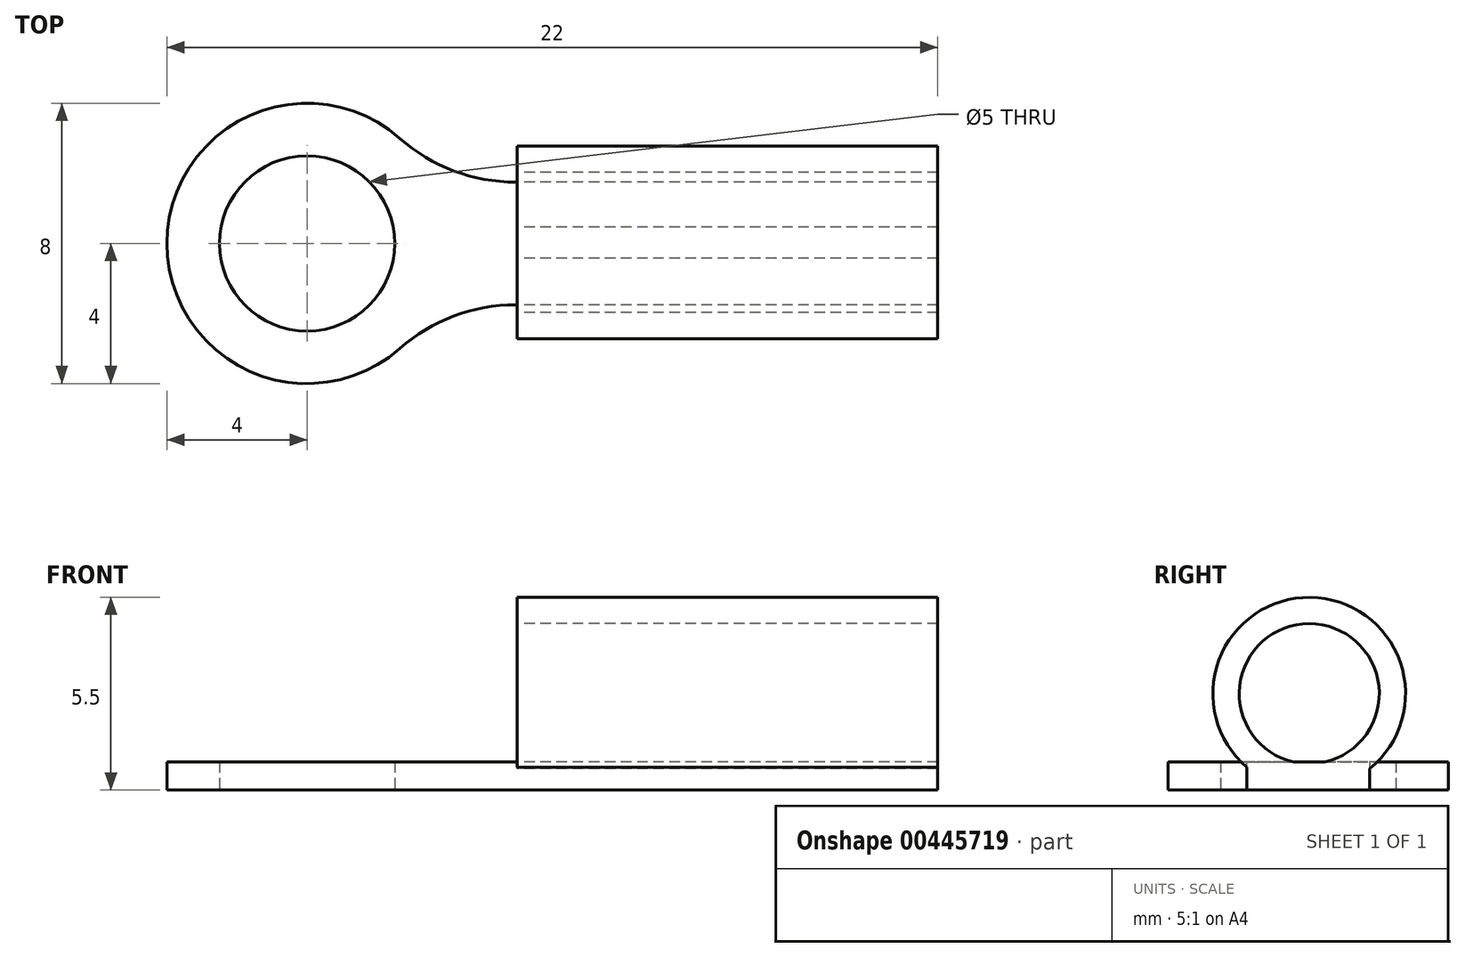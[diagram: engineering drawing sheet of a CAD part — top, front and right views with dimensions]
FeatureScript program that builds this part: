
annotation { "Feature Type Name" : "Feature", "Feature Type Description" : "" }
export const myFeature = defineFeature(function(context is Context, id is Id, definition is map)
    precondition{}
    {
        {
            var Q0;
            Q0=qCreatedBy(makeId("Top.planeOp"),FACE);
            var sketch = newSketch(context, id + "F0", { "sketchPlane" : qUnion([Q0])});
            skCircle(sketch, "E0", {"center": v(0, 0) * mm, "radius": 2.5 * mm});
            skArc(sketch, "E1", {"start": v(2.65, 3) * mm, "mid": v(-4, 0) * mm, "end": v(2.65, -3) * mm});
            skLineSegment(sketch, "E2.bottom", {"start": v(18, 1.75) * mm, "end": v(5.95, 1.75) * mm});
            skLineSegment(sketch, "E2.top", {"start": v(18, -1.75) * mm, "end": v(5.95, -1.75) * mm});
            skLineSegment(sketch, "E2.left", {"start": v(18, 1.75) * mm, "end": v(18, -1.75) * mm});
            skPoint(sketch, "E2.right.end.orphan", {"position": v(-18, -1.75) * mm});
            skPoint(sketch, "E2.right.start.orphan", {"position": v(-18, 1.75) * mm});
            skPoint(sketch, "E3.visualSharp", {"position": v(3.6, 1.75) * mm});
            skArc(sketch, "E3.filletArc", {"start": v(2.65, 3) * mm, "mid": v(4.19, 2.07) * mm, "end": v(5.95, 1.75) * mm});
            skPoint(sketch, "E4.visualSharp", {"position": v(3.6, -1.75) * mm});
            skArc(sketch, "E4.filletArc", {"start": v(5.95, -1.75) * mm, "mid": v(4.19, -2.07) * mm, "end": v(2.65, -3) * mm});
            skSolve(sketch);
        }
        {
            var Q0;
            Q0=makeQuery(id+"F0.imprint","IMPRINT",FACE,{"disambiguationData":[TD([[makeQuery(id+"F0.imprint","IMPRINT",EDGE,{"derivedFrom":sQuery(id+"F0.wireOp",EDGE,"E0")}),-1.0]])]});
            extrude(context, id + "F1", {"entities" : qUnion([Q0]), "depth" : 0.8 * mm});
        }
        {
            var Q0;
            Q0=qCreatedBy(makeId("Right.planeOp"),FACE);
            var sketch = newSketch(context, id + "F2", { "sketchPlane" : qUnion([Q0])});
            skCircle(sketch, "E5", {"center": v(0.02, 2.75) * mm, "radius": 2.75 * mm});
            skPoint(sketch, "E5.first.point", {"position": v(0, 0) * mm});
            skPoint(sketch, "E5.second.point", {"position": v(-2.1, 1) * mm});
            skPoint(sketch, "E5.third.point", {"position": v(2.11, 0.96) * mm});
            skCircle(sketch, "E6", {"center": v(0.02, 2.75) * mm, "radius": 2 * mm});
            skSolve(sketch);
        }
        {
            var Q0;
            Q0=makeQuery(id+"F2.imprint","IMPRINT",FACE,{"disambiguationData":[TD([[makeQuery(id+"F2.imprint","IMPRINT",EDGE,{"derivedFrom":sQuery(id+"F2.wireOp",EDGE,"E5")}),1.0]])]});
            extrude(context, id + "F3", {"entities" : qUnion([Q0]), "operationType" : NewBodyOperationType.ADD, "depth" : 18 * mm, "hasSecondDirection" : true, "secondDirectionOppositeDirection" : false, "secondDirectionDepth" : 6 * mm});
        }
    });
